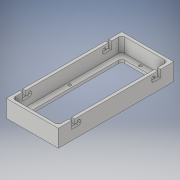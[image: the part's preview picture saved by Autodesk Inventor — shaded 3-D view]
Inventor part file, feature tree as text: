
AUTODESK INVENTOR PART (.ipt)
format: ipt  version: 2017 (Build 210142000, 142)  size: 280,576 bytes
history: native  units: in
note: dims shown in document units (in); Inventor stores cm internally (conversion verified against a paired STEP export)
features: extrude x4, sketch x3, fillet x3, plane x2, mirror x1, projected_geometry x1
ambient origin geometry x8: Origin, YZ Plane, XZ Plane, XY Plane, X Axis, Y Axis, Z Axis, Center Point
bodies: Solid1 (feature_tree)
feature tree (14):
  extrude  "Extrusion1"  Depth=0.125in
  sketch  "Sketch2"  dims[d2=0.125in d3=0.125in]
  extrude  "Extrusion9"  Depth=0.125in
  extrude  "Extrusion10"  Depth=0.125in
  extrude  "Extrusion11"  Depth=0.125in
  fillet  "Fillet1"  Radius=0.25in
  fillet  "Fillet2"  Radius=0.25in
  fillet  "Fillet3"  Radius=0.125in
  plane  "Work Plane1"
  mirror  "Mirror1"
  sketch  "Sketch9"  dims[d7=0.25in d8=0.125in]
  sketch  "Sketch10"  dims[d9=0.125in d10=0.125in d11=0.125in d12=0.25in d13=0.25in d14=0.125in d15=0.125in d16=0.25in d17=0.25in d18=0.125in d19=0.75in d20=0.0in d121=0.574in d154=1.0in d155=0.0in d156=0.25in d157=0.25in d158=0.25in d159=0.25in d160=0.125in d161=0.0in d163=0.125in d166=0.125in d167=4.75in d168=2.375in d169=0.125in d170=0.0625in d171=2.375in d172=0.125in d173=0.125in d174=1.75in d175=0.875in d176=0.125in d177=0.125in d178=0.9375in d179=0.125in d180=0.0in d181=0.125in d182=0.125in d183=0.125in d190=0.125in d191=0.125in d192=0.125in d193=0.125in d194=0.1in d195=0.1in d196=0.0625in d197=0.0625in]
  projected_geometry  "Projected Loop2"
  plane  "Work Plane2"
